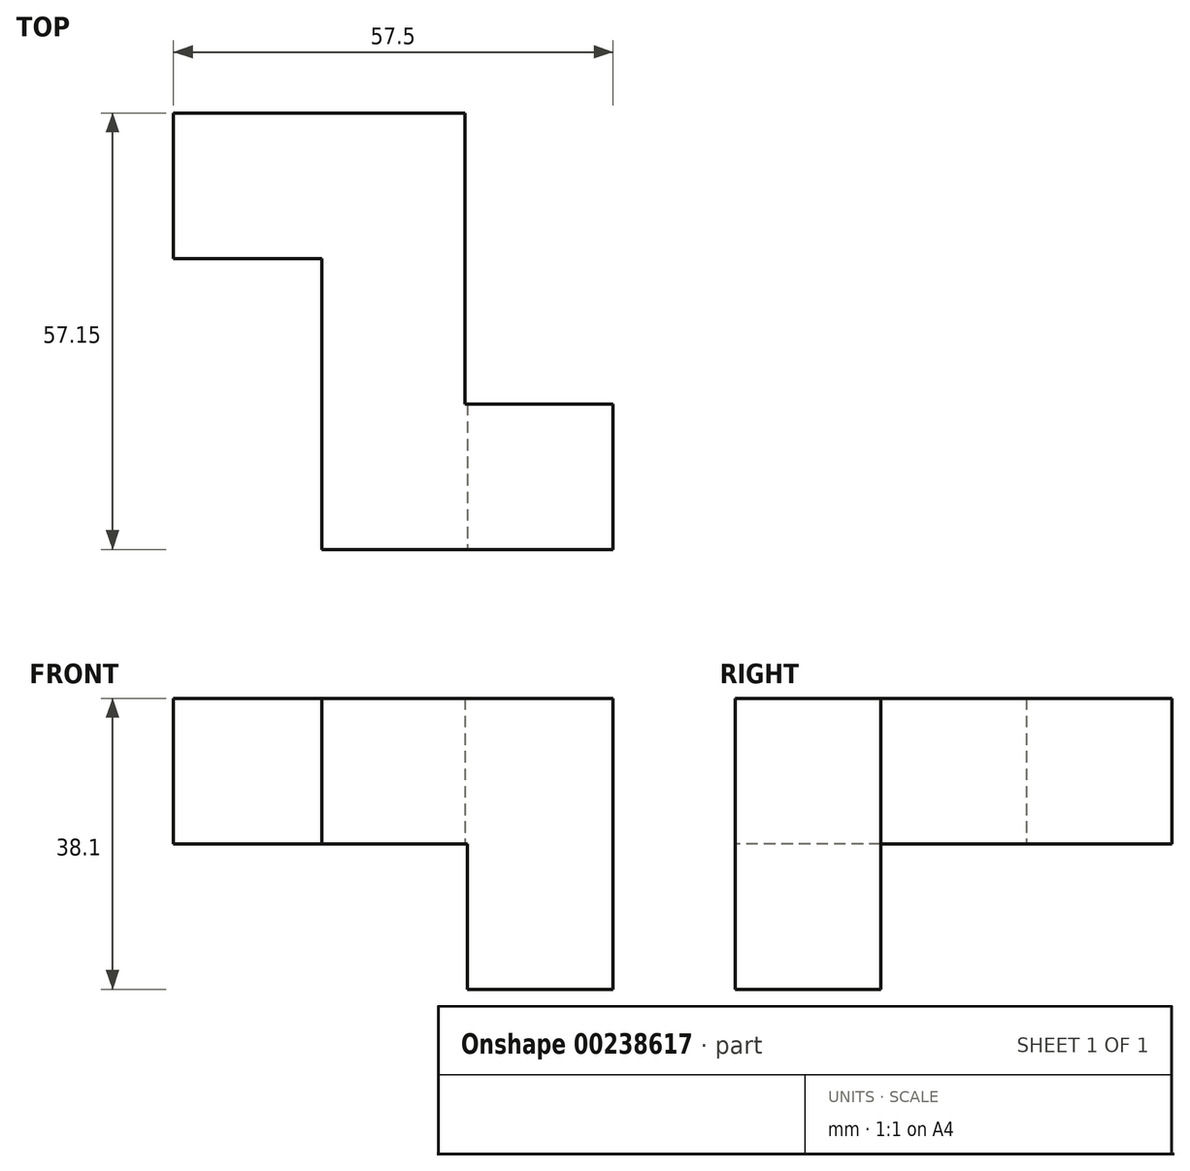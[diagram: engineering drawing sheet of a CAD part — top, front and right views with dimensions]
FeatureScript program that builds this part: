
annotation { "Feature Type Name" : "Feature", "Feature Type Description" : "" }
export const myFeature = defineFeature(function(context is Context, id is Id, definition is map)
    precondition{}
    {
        {
            var Q0;
            Q0=qCreatedBy(makeId("Top.planeOp"),FACE);
            var sketch = newSketch(context, id + "F0", { "sketchPlane" : qUnion([Q0])});
            skLineSegment(sketch, "E0", {"start": v(0, 0) * mm, "end": v(0, 19.05) * mm});
            skLineSegment(sketch, "E1", {"start": v(0, 19.05) * mm, "end": v(38.1, 19.05) * mm});
            skLineSegment(sketch, "E2", {"start": v(38.1, 19.05) * mm, "end": v(38.1, -19.05) * mm});
            skLineSegment(sketch, "E3", {"start": v(38.1, -19.05) * mm, "end": v(57.5, -19.05) * mm});
            skLineSegment(sketch, "E4", {"start": v(57.5, -19.05) * mm, "end": v(57.5, -38.1) * mm});
            skLineSegment(sketch, "E5", {"start": v(57.5, -38.1) * mm, "end": v(19.4, -38.1) * mm});
            skLineSegment(sketch, "E6", {"start": v(19.4, -38.1) * mm, "end": v(19.4, 0) * mm});
            skLineSegment(sketch, "E7", {"start": v(19.4, 0) * mm, "end": v(0, 0) * mm});
            skSolve(sketch);
        }
        {
            var Q0;
            Q0 = qSketchRegion(id + "F0", true);
            extrude(context, id + "F1", {"entities" : qUnion([Q0]), "depth" : 19.05 * mm});
        }
        {
            var Q0;
            Q0=makeQuery(id+"F1.opExtrude","CAP_FACE",FACE,{"disambiguationData":[OSD([sQuery(id+"F0.wireOp",EDGE,"E0"),sQuery(id+"F0.wireOp",EDGE,"E1"),sQuery(id+"F0.wireOp",EDGE,"E2"),sQuery(id+"F0.wireOp",EDGE,"E3"),sQuery(id+"F0.wireOp",EDGE,"E4"),sQuery(id+"F0.wireOp",EDGE,"E5"),sQuery(id+"F0.wireOp",EDGE,"E6"),sQuery(id+"F0.wireOp",EDGE,"E7")])],"isStart":true});
            var sketch = newSketch(context, id + "F2", { "sketchPlane" : qUnion([Q0])});
            skLineSegment(sketch, "E8.bottom", {"start": v(57.5, 19.05) * mm, "end": v(38.45, 19.05) * mm});
            skLineSegment(sketch, "E8.top", {"start": v(57.5, 38.1) * mm, "end": v(38.45, 38.1) * mm});
            skLineSegment(sketch, "E8.left", {"start": v(57.5, 19.05) * mm, "end": v(57.5, 38.1) * mm});
            skLineSegment(sketch, "E8.right", {"start": v(38.45, 19.05) * mm, "end": v(38.45, 38.1) * mm});
            skSolve(sketch);
        }
        {
            var Q0;
            Q0 = qSketchRegion(id + "F2", true);
            extrude(context, id + "F3", {"entities" : qUnion([Q0]), "operationType" : NewBodyOperationType.ADD, "depth" : 19.05 * mm});
        }
    });
